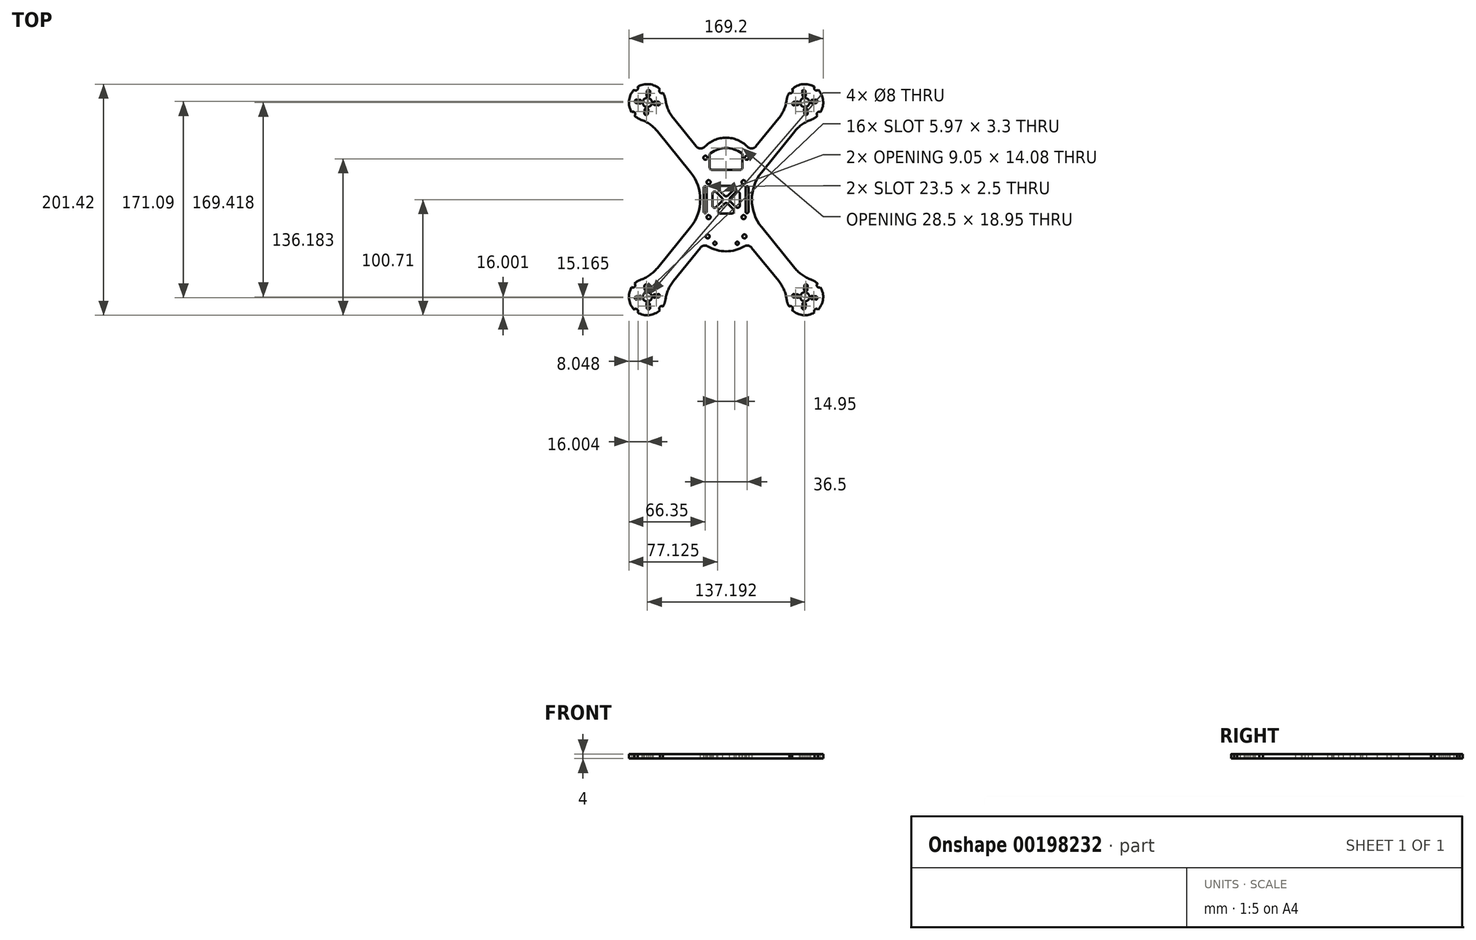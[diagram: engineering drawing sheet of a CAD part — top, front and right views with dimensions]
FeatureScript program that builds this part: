
annotation { "Feature Type Name" : "Feature", "Feature Type Description" : "" }
export const myFeature = defineFeature(function(context is Context, id is Id, definition is map)
    precondition{}
    {
        {
            var Q0;
            Q0=qCreatedBy(makeId("Top.planeOp"),FACE);
            var sketch = newSketch(context, id + "F0", { "sketchPlane" : qUnion([Q0])});
            skCircle(sketch, "E0", {"center": v(0, 0) * mm, "radius": 109 * mm, "construction": true});
            skCircle(sketch, "E1", {"center": v(68.6, 84.7) * mm, "radius": 63.5 * mm, "construction": true});
            skLineSegment(sketch, "E2", {"start": v(0, 0) * mm, "end": v(68.6, 84.7) * mm, "construction": true});
            skArc(sketch, "E3", {"start": v(73.98, 69.64) * mm, "mid": v(77.02, 71.1) * mm, "end": v(79.68, 73.17) * mm});
            skLineSegment(sketch, "E4", {"start": v(30.95, 23.91) * mm, "end": v(59.88, 59.65) * mm});
            skLineSegment(sketch, "E5", {"start": v(45.9, 70.98) * mm, "end": v(26.08, 46.5) * mm});
            skPoint(sketch, "E6.visualSharp", {"position": v(53.28, 80.1) * mm});
            skArc(sketch, "E6.filletArc", {"start": v(45.9, 70.98) * mm, "mid": v(50.4, 78.44) * mm, "end": v(52.74, 86.84) * mm});
            skPoint(sketch, "E7.visualSharp", {"position": v(67.27, 68.76) * mm});
            skArc(sketch, "E7.filletArc", {"start": v(73.98, 69.64) * mm, "mid": v(66.24, 65.61) * mm, "end": v(59.88, 59.65) * mm});
            skCircle(sketch, "E8", {"center": v(68.6, 84.7) * mm, "radius": 4 * mm});
            skLineSegment(sketch, "E9", {"start": v(0, 109) * mm, "end": v(0, 0) * mm, "construction": true});
            skLineSegment(sketch, "E10", {"start": v(0, 0) * mm, "end": v(109, 0) * mm, "construction": true});
            skArc(sketch, "E11.MirrorCS", {"start": v(-73.98, 69.64) * mm, "mid": v(-66.24, 65.61) * mm, "end": v(-59.88, 59.65) * mm});
            skArc(sketch, "E12.MirrorCS", {"start": v(-45.9, 70.98) * mm, "mid": v(-50.4, 78.44) * mm, "end": v(-52.74, 86.84) * mm});
            skPoint(sketch, "E13.MirrorP", {"position": v(-67.27, 68.76) * mm});
            skPoint(sketch, "E14.MirrorP", {"position": v(-53.28, 80.1) * mm});
            skArc(sketch, "E15.MirrorCS", {"start": v(-73.98, 69.64) * mm, "mid": v(-77.02, 71.1) * mm, "end": v(-79.68, 73.17) * mm});
            skLineSegment(sketch, "E16.MirrorCS", {"start": v(-30.95, 23.91) * mm, "end": v(-59.88, 59.65) * mm});
            skLineSegment(sketch, "E17.MirrorCS", {"start": v(-45.9, 70.98) * mm, "end": v(-26.08, 46.5) * mm});
            skCircle(sketch, "E18.MirrorC", {"center": v(-68.6, 84.7) * mm, "radius": 4 * mm});
            skCircle(sketch, "E19.MirrorC", {"center": v(-68.6, 84.7) * mm, "radius": 63.5 * mm, "construction": true});
            skLineSegment(sketch, "E20.MirrorCS", {"start": v(0, 0) * mm, "end": v(-68.6, 84.7) * mm, "construction": true});
            skArc(sketch, "E21.MirrorCS", {"start": v(-73.98, -69.64) * mm, "mid": v(-66.24, -65.61) * mm, "end": v(-59.88, -59.65) * mm});
            skArc(sketch, "E22.MirrorCS", {"start": v(-45.9, -70.98) * mm, "mid": v(-50.4, -78.44) * mm, "end": v(-52.74, -86.84) * mm});
            skPoint(sketch, "E23.MirrorP", {"position": v(-53.28, -80.1) * mm});
            skArc(sketch, "E24.MirrorCS", {"start": v(-73.98, -69.64) * mm, "mid": v(-77.02, -71.1) * mm, "end": v(-79.68, -73.17) * mm});
            skPoint(sketch, "E25.MirrorP", {"position": v(-67.27, -68.76) * mm});
            skCircle(sketch, "E26.MirrorC", {"center": v(-68.6, -84.7) * mm, "radius": 4 * mm});
            skLineSegment(sketch, "E27.MirrorCS", {"start": v(-30.95, -23.91) * mm, "end": v(-59.88, -59.65) * mm});
            skArc(sketch, "E28.MirrorCS", {"start": v(45.9, -70.98) * mm, "mid": v(50.4, -78.44) * mm, "end": v(52.74, -86.84) * mm});
            skArc(sketch, "E29.MirrorCS", {"start": v(73.98, -69.64) * mm, "mid": v(66.24, -65.61) * mm, "end": v(59.88, -59.65) * mm});
            skCircle(sketch, "E30.MirrorC", {"center": v(68.6, -84.7) * mm, "radius": 4 * mm});
            skPoint(sketch, "E31.MirrorP", {"position": v(67.27, -68.76) * mm});
            skArc(sketch, "E32.MirrorCS", {"start": v(73.98, -69.64) * mm, "mid": v(77.02, -71.1) * mm, "end": v(79.68, -73.17) * mm});
            skPoint(sketch, "E33.MirrorP", {"position": v(53.28, -80.1) * mm});
            skCircle(sketch, "E34.MirrorC", {"center": v(68.6, -84.7) * mm, "radius": 63.5 * mm, "construction": true});
            skCircle(sketch, "E35.MirrorC", {"center": v(-68.6, -84.7) * mm, "radius": 63.5 * mm, "construction": true});
            skLineSegment(sketch, "E36.MirrorCS", {"start": v(30.95, -23.91) * mm, "end": v(59.88, -59.65) * mm});
            skLineSegment(sketch, "E37.MirrorCS", {"start": v(0, 0) * mm, "end": v(-68.6, -84.7) * mm, "construction": true});
            skLineSegment(sketch, "E38.MirrorCS", {"start": v(0, 0) * mm, "end": v(68.6, -84.7) * mm, "construction": true});
            skCircle(sketch, "E39", {"center": v(-15.25, -15.25) * mm, "radius": 1.75 * mm});
            skCircle(sketch, "E40", {"center": v(15.25, -15.25) * mm, "radius": 1.75 * mm});
            skCircle(sketch, "E41.MirrorC", {"center": v(15.25, 15.25) * mm, "radius": 1.75 * mm});
            skCircle(sketch, "E42.MirrorC", {"center": v(-15.25, 15.25) * mm, "radius": 1.75 * mm});
            skLineSegment(sketch, "E43", {"start": v(-12.25, 26) * mm, "end": v(12.25, 26) * mm});
            skLineSegment(sketch, "E44", {"start": v(-14.25, 28) * mm, "end": v(-14.25, 39) * mm});
            skLineSegment(sketch, "E45", {"start": v(14.25, 28) * mm, "end": v(14.25, 39) * mm});
            skArc(sketch, "E46", {"start": v(18.61, 46.16) * mm, "mid": v(0, 54) * mm, "end": v(-18.61, 46.16) * mm});
            skPoint(sketch, "E47.visualSharp", {"position": v(-22.14, 41.64) * mm});
            skArc(sketch, "E47.filletArc", {"start": v(-26.08, 46.5) * mm, "mid": v(-22.42, 44.65) * mm, "end": v(-18.61, 46.16) * mm});
            skPoint(sketch, "E48.visualSharp", {"position": v(22.14, 41.64) * mm});
            skArc(sketch, "E48.filletArc", {"start": v(18.61, 46.16) * mm, "mid": v(22.42, 44.65) * mm, "end": v(26.08, 46.5) * mm});
            skPoint(sketch, "E49.visualSharp", {"position": v(-14.25, 26) * mm});
            skArc(sketch, "E49.filletArc", {"start": v(-14.25, 28) * mm, "mid": v(-13.66, 26.59) * mm, "end": v(-12.25, 26) * mm});
            skPoint(sketch, "E50.visualSharp", {"position": v(14.25, 26) * mm});
            skArc(sketch, "E50.filletArc", {"start": v(12.25, 26) * mm, "mid": v(13.66, 26.59) * mm, "end": v(14.25, 28) * mm});
            skPoint(sketch, "E51.visualSharp", {"position": v(-14.25, 40) * mm});
            skPoint(sketch, "E52.visualSharp", {"position": v(14.25, 44) * mm});
            skArc(sketch, "E53", {"start": v(-30.95, -23.91) * mm, "mid": v(-22.48, 0) * mm, "end": v(-30.95, 23.91) * mm});
            skArc(sketch, "E54.MirrorCS", {"start": v(30.95, -23.91) * mm, "mid": v(22.48, 0) * mm, "end": v(30.95, 23.91) * mm});
            skLineSegment(sketch, "E55", {"start": v(-45.9, -70.98) * mm, "end": v(-22.27, -41.8) * mm});
            skLineSegment(sketch, "E56", {"start": v(45.9, -70.98) * mm, "end": v(22.27, -41.8) * mm});
            skCircle(sketch, "E57", {"center": v(-16, -32) * mm, "radius": 1.75 * mm});
            skCircle(sketch, "E58.MirrorC", {"center": v(16, -32) * mm, "radius": 1.75 * mm});
            skCircle(sketch, "E59", {"center": v(-18, 36.5) * mm, "radius": 1.75 * mm});
            skCircle(sketch, "E60.MirrorC", {"center": v(18, 36.5) * mm, "radius": 1.75 * mm});
            skLineSegment(sketch, "E61.bottom", {"start": v(-19.5, 10.5) * mm, "end": v(-17, 10.5) * mm, "construction": true});
            skLineSegment(sketch, "E61.top", {"start": v(-19.5, -10.5) * mm, "end": v(-17, -10.5) * mm, "construction": true});
            skLineSegment(sketch, "E61.left", {"start": v(-19.5, 10.5) * mm, "end": v(-19.5, -10.5) * mm});
            skLineSegment(sketch, "E61.right", {"start": v(-17, 10.5) * mm, "end": v(-17, -10.5) * mm});
            skArc(sketch, "E62", {"start": v(-17, 10.5) * mm, "mid": v(-18.25, 11.75) * mm, "end": v(-19.5, 10.5) * mm});
            skArc(sketch, "E63", {"start": v(-19.5, -10.5) * mm, "mid": v(-18.25, -11.75) * mm, "end": v(-17, -10.5) * mm});
            skArc(sketch, "E64.MirrorCS", {"start": v(19.5, -10.5) * mm, "mid": v(18.25, -11.75) * mm, "end": v(17, -10.5) * mm});
            skLineSegment(sketch, "E65.MirrorCS", {"start": v(19.5, 10.5) * mm, "end": v(17, 10.5) * mm, "construction": true});
            skLineSegment(sketch, "E66.MirrorCS", {"start": v(19.5, -10.5) * mm, "end": v(17, -10.5) * mm, "construction": true});
            skLineSegment(sketch, "E67.MirrorCS", {"start": v(19.5, 10.5) * mm, "end": v(19.5, -10.5) * mm});
            skLineSegment(sketch, "E68.MirrorCS", {"start": v(17, 10.5) * mm, "end": v(17, -10.5) * mm});
            skArc(sketch, "E69.MirrorCS", {"start": v(17, 10.5) * mm, "mid": v(18.25, 11.75) * mm, "end": v(19.5, 10.5) * mm});
            skArc(sketch, "E70", {"start": v(-77.04, -98.3) * mm, "mid": v(-77.4, -95.59) * mm, "end": v(-80.14, -95.79) * mm});
            skArc(sketch, "E71", {"start": v(-82.19, -76.27) * mm, "mid": v(-79.48, -75.9) * mm, "end": v(-79.68, -73.17) * mm});
            skArc(sketch, "E72", {"start": v(-55, -93.15) * mm, "mid": v(-57.72, -93.52) * mm, "end": v(-57.51, -96.25) * mm});
            skLineSegment(sketch, "E73", {"start": v(-81.03, -74.64) * mm, "end": v(-56.16, -94.78) * mm, "construction": true});
            skArc(sketch, "E74.MirrorC", {"start": v(77.04, -98.3) * mm, "mid": v(77.4, -95.59) * mm, "end": v(80.14, -95.79) * mm});
            skArc(sketch, "E75.MirrorC", {"start": v(82.19, -76.27) * mm, "mid": v(79.48, -75.9) * mm, "end": v(79.68, -73.17) * mm});
            skArc(sketch, "E76.MirrorC", {"start": v(55, -93.15) * mm, "mid": v(57.72, -93.52) * mm, "end": v(57.51, -96.25) * mm});
            skArc(sketch, "E77.MirrorC", {"start": v(-82.19, 76.27) * mm, "mid": v(-79.48, 75.9) * mm, "end": v(-79.68, 73.17) * mm});
            skArc(sketch, "E78.MirrorC", {"start": v(-77.04, 98.3) * mm, "mid": v(-77.4, 95.59) * mm, "end": v(-80.14, 95.79) * mm});
            skArc(sketch, "E79.MirrorC", {"start": v(-55, 93.15) * mm, "mid": v(-57.72, 93.52) * mm, "end": v(-57.51, 96.25) * mm});
            skArc(sketch, "E80.MirrorC", {"start": v(82.19, 76.27) * mm, "mid": v(79.48, 75.9) * mm, "end": v(79.68, 73.17) * mm});
            skArc(sketch, "E81.MirrorC", {"start": v(77.04, 98.3) * mm, "mid": v(77.4, 95.59) * mm, "end": v(80.14, 95.79) * mm});
            skArc(sketch, "E82.MirrorC", {"start": v(55, 93.15) * mm, "mid": v(57.72, 93.52) * mm, "end": v(57.51, 96.25) * mm});
            skArc(sketch, "E83.trimOffspring", {"start": v(-77.04, 98.3) * mm, "mid": v(-66.92, 100.62) * mm, "end": v(-57.51, 96.25) * mm});
            skArc(sketch, "E84.trimOffspring", {"start": v(-82.19, 76.27) * mm, "mid": v(-84.5, 86.38) * mm, "end": v(-80.14, 95.79) * mm});
            skArc(sketch, "E85.trimOffspring", {"start": v(-55, 93.15) * mm, "mid": v(-53.54, 90.12) * mm, "end": v(-52.74, 86.84) * mm});
            skArc(sketch, "E86.trimOffspring", {"start": v(77.04, 98.3) * mm, "mid": v(66.92, 100.62) * mm, "end": v(57.51, 96.25) * mm});
            skArc(sketch, "E87.trimOffspring", {"start": v(55, 93.15) * mm, "mid": v(53.54, 90.12) * mm, "end": v(52.74, 86.84) * mm});
            skArc(sketch, "E88.trimOffspring", {"start": v(82.19, 76.27) * mm, "mid": v(84.5, 86.38) * mm, "end": v(80.14, 95.79) * mm});
            skArc(sketch, "E89.trimOffspring", {"start": v(-55.46, -93.84) * mm, "mid": v(-53.68, -90.5) * mm, "end": v(-52.74, -86.84) * mm});
            skArc(sketch, "E90.trimOffspring", {"start": v(-77.04, -98.3) * mm, "mid": v(-66.92, -100.62) * mm, "end": v(-57.51, -96.25) * mm});
            skLineSegment(sketch, "E91", {"start": v(-68.6, -84.7) * mm, "end": v(-78.67, -97.14) * mm, "construction": true});
            skArc(sketch, "E92.trimOffspring", {"start": v(-82.19, -76.27) * mm, "mid": v(-84.5, -86.38) * mm, "end": v(-80.14, -95.79) * mm});
            skArc(sketch, "E93.trimOffspring", {"start": v(82.19, -76.27) * mm, "mid": v(84.5, -86.38) * mm, "end": v(80.14, -95.79) * mm});
            skArc(sketch, "E94.trimOffspring", {"start": v(55, -93.15) * mm, "mid": v(53.54, -90.12) * mm, "end": v(52.74, -86.84) * mm});
            skArc(sketch, "E95.trimOffspring", {"start": v(77.04, -98.3) * mm, "mid": v(66.92, -100.62) * mm, "end": v(57.51, -96.25) * mm});
            skArc(sketch, "E96", {"start": v(13.42, 40.63) * mm, "mid": v(0, 44.95) * mm, "end": v(-13.42, 40.63) * mm});
            skArc(sketch, "E97.filletArc", {"start": v(-13.42, 40.63) * mm, "mid": v(-14.03, 39.92) * mm, "end": v(-14.25, 39) * mm});
            skPoint(sketch, "E98.visualSharp", {"position": v(14.25, 40) * mm});
            skArc(sketch, "E98.filletArc", {"start": v(14.25, 39) * mm, "mid": v(14.03, 39.92) * mm, "end": v(13.42, 40.63) * mm});
            skLineSegment(sketch, "E99", {"start": v(68.6, -84.7) * mm, "end": v(70.27, -68.8) * mm, "construction": true});
            skArc(sketch, "E100", {"start": v(67.78, -78.09) * mm, "mid": v(69.12, -79.74) * mm, "end": v(70.77, -78.4) * mm});
            skArc(sketch, "E101", {"start": v(71.08, -75.42) * mm, "mid": v(69.75, -73.77) * mm, "end": v(68.1, -75.1) * mm});
            skLineSegment(sketch, "E102", {"start": v(70.77, -78.4) * mm, "end": v(71.08, -75.42) * mm});
            skLineSegment(sketch, "E103", {"start": v(67.78, -78.09) * mm, "end": v(68.1, -75.1) * mm});
            skArc(sketch, "E104.1.0", {"start": v(61.97, -85.52) * mm, "mid": v(63.62, -84.19) * mm, "end": v(62.29, -82.54) * mm});
            skLineSegment(sketch, "E104.1.1", {"start": v(61.97, -85.52) * mm, "end": v(59, -85.2) * mm});
            skArc(sketch, "E104.1.2", {"start": v(59.3, -82.22) * mm, "mid": v(57.66, -83.56) * mm, "end": v(59, -85.2) * mm});
            skLineSegment(sketch, "E104.1.3", {"start": v(62.29, -82.54) * mm, "end": v(59.3, -82.22) * mm});
            skLineSegment(sketch, "E104.1.4", {"start": v(68.6, -84.7) * mm, "end": v(52.68, -83.04) * mm, "construction": true});
            skArc(sketch, "E104.2.0", {"start": v(69.4, -91.33) * mm, "mid": v(68.07, -89.68) * mm, "end": v(66.42, -91.02) * mm});
            skLineSegment(sketch, "E104.2.1", {"start": v(69.4, -91.33) * mm, "end": v(69.1, -94.31) * mm});
            skArc(sketch, "E104.2.2", {"start": v(66.11, -94) * mm, "mid": v(67.45, -95.65) * mm, "end": v(69.1, -94.31) * mm});
            skLineSegment(sketch, "E104.2.3", {"start": v(66.42, -91.02) * mm, "end": v(66.11, -94) * mm});
            skLineSegment(sketch, "E104.2.4", {"start": v(68.6, -84.7) * mm, "end": v(66.92, -100.62) * mm, "construction": true});
            skArc(sketch, "E104.3.0", {"start": v(75.22, -83.9) * mm, "mid": v(73.57, -85.23) * mm, "end": v(74.9, -86.88) * mm});
            skLineSegment(sketch, "E104.3.1", {"start": v(75.22, -83.9) * mm, "end": v(78.2, -84.21) * mm});
            skArc(sketch, "E104.3.2", {"start": v(77.89, -87.2) * mm, "mid": v(79.54, -85.86) * mm, "end": v(78.2, -84.21) * mm});
            skLineSegment(sketch, "E104.3.3", {"start": v(74.9, -86.88) * mm, "end": v(77.89, -87.2) * mm});
            skLineSegment(sketch, "E104.3.4", {"start": v(68.6, -84.7) * mm, "end": v(84.5, -86.38) * mm, "construction": true});
            skLineSegment(sketch, "E105.MirrorCS", {"start": v(-69.4, -91.33) * mm, "end": v(-69.1, -94.31) * mm});
            skArc(sketch, "E106.MirrorCS", {"start": v(-69.4, -91.33) * mm, "mid": v(-68.07, -89.68) * mm, "end": v(-66.42, -91.02) * mm});
            skLineSegment(sketch, "E107.MirrorCS", {"start": v(-66.42, -91.02) * mm, "end": v(-66.11, -94) * mm});
            skArc(sketch, "E108.MirrorCS", {"start": v(-66.11, -94) * mm, "mid": v(-67.45, -95.65) * mm, "end": v(-69.1, -94.31) * mm});
            skLineSegment(sketch, "E109.MirrorCS", {"start": v(-68.6, -84.7) * mm, "end": v(-66.92, -100.62) * mm, "construction": true});
            skLineSegment(sketch, "E110.MirrorCS", {"start": v(-68.6, -84.7) * mm, "end": v(-84.5, -86.38) * mm, "construction": true});
            skLineSegment(sketch, "E111.MirrorCS", {"start": v(-68.6, -84.7) * mm, "end": v(-52.68, -83.04) * mm, "construction": true});
            skLineSegment(sketch, "E112.MirrorCS", {"start": v(-68.6, -84.7) * mm, "end": v(-70.27, -68.8) * mm, "construction": true});
            skLineSegment(sketch, "E113.MirrorCS", {"start": v(-70.77, -78.4) * mm, "end": v(-71.08, -75.42) * mm});
            skLineSegment(sketch, "E114.MirrorCS", {"start": v(-67.78, -78.09) * mm, "end": v(-68.1, -75.1) * mm});
            skArc(sketch, "E115.MirrorCS", {"start": v(-71.08, -75.42) * mm, "mid": v(-69.75, -73.77) * mm, "end": v(-68.1, -75.1) * mm});
            skArc(sketch, "E116.MirrorCS", {"start": v(-67.78, -78.09) * mm, "mid": v(-69.12, -79.74) * mm, "end": v(-70.77, -78.4) * mm});
            skLineSegment(sketch, "E117.MirrorCS", {"start": v(-75.22, -83.9) * mm, "end": v(-78.2, -84.21) * mm});
            skArc(sketch, "E118.MirrorCS", {"start": v(-77.89, -87.2) * mm, "mid": v(-79.54, -85.86) * mm, "end": v(-78.2, -84.21) * mm});
            skLineSegment(sketch, "E119.MirrorCS", {"start": v(-74.9, -86.88) * mm, "end": v(-77.89, -87.2) * mm});
            skArc(sketch, "E120.MirrorCS", {"start": v(-75.22, -83.9) * mm, "mid": v(-73.57, -85.23) * mm, "end": v(-74.9, -86.88) * mm});
            skLineSegment(sketch, "E121.MirrorCS", {"start": v(-61.97, -85.52) * mm, "end": v(-59, -85.2) * mm});
            skArc(sketch, "E122.MirrorCS", {"start": v(-59.3, -82.22) * mm, "mid": v(-57.66, -83.56) * mm, "end": v(-59, -85.2) * mm});
            skLineSegment(sketch, "E123.MirrorCS", {"start": v(-62.29, -82.54) * mm, "end": v(-59.3, -82.22) * mm});
            skArc(sketch, "E124.MirrorCS", {"start": v(-61.97, -85.52) * mm, "mid": v(-63.62, -84.19) * mm, "end": v(-62.29, -82.54) * mm});
            skArc(sketch, "E125.MirrorCS", {"start": v(-75.22, 83.9) * mm, "mid": v(-73.57, 85.23) * mm, "end": v(-74.9, 86.88) * mm});
            skLineSegment(sketch, "E126.MirrorCS", {"start": v(-74.9, 86.88) * mm, "end": v(-77.89, 87.2) * mm});
            skArc(sketch, "E127.MirrorCS", {"start": v(-77.89, 87.2) * mm, "mid": v(-79.54, 85.86) * mm, "end": v(-78.2, 84.21) * mm});
            skLineSegment(sketch, "E128.MirrorCS", {"start": v(-75.22, 83.9) * mm, "end": v(-78.2, 84.21) * mm});
            skLineSegment(sketch, "E129.MirrorCS", {"start": v(-68.6, 84.7) * mm, "end": v(-84.5, 86.38) * mm, "construction": true});
            skLineSegment(sketch, "E130.MirrorCS", {"start": v(-68.6, 84.7) * mm, "end": v(-70.27, 68.8) * mm, "construction": true});
            skLineSegment(sketch, "E131.MirrorCS", {"start": v(-68.6, 84.7) * mm, "end": v(-52.68, 83.04) * mm, "construction": true});
            skLineSegment(sketch, "E132.MirrorCS", {"start": v(-68.6, 84.7) * mm, "end": v(-66.92, 100.62) * mm, "construction": true});
            skArc(sketch, "E133.MirrorCS", {"start": v(-67.78, 78.09) * mm, "mid": v(-69.12, 79.74) * mm, "end": v(-70.77, 78.4) * mm});
            skLineSegment(sketch, "E134.MirrorCS", {"start": v(-70.77, 78.4) * mm, "end": v(-71.08, 75.42) * mm});
            skLineSegment(sketch, "E135.MirrorCS", {"start": v(-67.78, 78.09) * mm, "end": v(-68.1, 75.1) * mm});
            skArc(sketch, "E136.MirrorCS", {"start": v(-71.08, 75.42) * mm, "mid": v(-69.75, 73.77) * mm, "end": v(-68.1, 75.1) * mm});
            skArc(sketch, "E137.MirrorCS", {"start": v(-61.97, 85.52) * mm, "mid": v(-63.62, 84.19) * mm, "end": v(-62.29, 82.54) * mm});
            skLineSegment(sketch, "E138.MirrorCS", {"start": v(-61.97, 85.52) * mm, "end": v(-59, 85.2) * mm});
            skLineSegment(sketch, "E139.MirrorCS", {"start": v(-62.29, 82.54) * mm, "end": v(-59.3, 82.22) * mm});
            skArc(sketch, "E140.MirrorCS", {"start": v(-59.3, 82.22) * mm, "mid": v(-57.66, 83.56) * mm, "end": v(-59, 85.2) * mm});
            skLineSegment(sketch, "E141.MirrorCS", {"start": v(-69.4, 91.33) * mm, "end": v(-69.1, 94.31) * mm});
            skArc(sketch, "E142.MirrorCS", {"start": v(-66.11, 94) * mm, "mid": v(-67.45, 95.65) * mm, "end": v(-69.1, 94.31) * mm});
            skLineSegment(sketch, "E143.MirrorCS", {"start": v(-66.42, 91.02) * mm, "end": v(-66.11, 94) * mm});
            skArc(sketch, "E144.MirrorCS", {"start": v(-69.4, 91.33) * mm, "mid": v(-68.07, 89.68) * mm, "end": v(-66.42, 91.02) * mm});
            skLineSegment(sketch, "E145.MirrorCS", {"start": v(66.42, 91.02) * mm, "end": v(66.11, 94) * mm});
            skArc(sketch, "E146.MirrorCS", {"start": v(66.11, 94) * mm, "mid": v(67.45, 95.65) * mm, "end": v(69.1, 94.31) * mm});
            skLineSegment(sketch, "E147.MirrorCS", {"start": v(69.4, 91.33) * mm, "end": v(69.1, 94.31) * mm});
            skArc(sketch, "E148.MirrorCS", {"start": v(69.4, 91.33) * mm, "mid": v(68.07, 89.68) * mm, "end": v(66.42, 91.02) * mm});
            skLineSegment(sketch, "E149.MirrorCS", {"start": v(75.22, 83.9) * mm, "end": v(78.2, 84.21) * mm});
            skArc(sketch, "E150.MirrorCS", {"start": v(77.89, 87.2) * mm, "mid": v(79.54, 85.86) * mm, "end": v(78.2, 84.21) * mm});
            skArc(sketch, "E151.MirrorCS", {"start": v(75.22, 83.9) * mm, "mid": v(73.57, 85.23) * mm, "end": v(74.9, 86.88) * mm});
            skLineSegment(sketch, "E152.MirrorCS", {"start": v(74.9, 86.88) * mm, "end": v(77.89, 87.2) * mm});
            skLineSegment(sketch, "E153.MirrorCS", {"start": v(70.77, 78.4) * mm, "end": v(71.08, 75.42) * mm});
            skArc(sketch, "E154.MirrorCS", {"start": v(71.08, 75.42) * mm, "mid": v(69.75, 73.77) * mm, "end": v(68.1, 75.1) * mm});
            skLineSegment(sketch, "E155.MirrorCS", {"start": v(68.6, 84.7) * mm, "end": v(70.27, 68.8) * mm, "construction": true});
            skLineSegment(sketch, "E156.MirrorCS", {"start": v(67.78, 78.09) * mm, "end": v(68.1, 75.1) * mm});
            skArc(sketch, "E157.MirrorCS", {"start": v(67.78, 78.09) * mm, "mid": v(69.12, 79.74) * mm, "end": v(70.77, 78.4) * mm});
            skArc(sketch, "E158.MirrorCS", {"start": v(59.3, 82.22) * mm, "mid": v(57.66, 83.56) * mm, "end": v(59, 85.2) * mm});
            skLineSegment(sketch, "E159.MirrorCS", {"start": v(62.29, 82.54) * mm, "end": v(59.3, 82.22) * mm});
            skLineSegment(sketch, "E160.MirrorCS", {"start": v(61.97, 85.52) * mm, "end": v(59, 85.2) * mm});
            skArc(sketch, "E161.MirrorCS", {"start": v(61.97, 85.52) * mm, "mid": v(63.62, 84.19) * mm, "end": v(62.29, 82.54) * mm});
            skLineSegment(sketch, "E162.MirrorCS", {"start": v(68.6, 84.7) * mm, "end": v(84.5, 86.38) * mm, "construction": true});
            skLineSegment(sketch, "E163.MirrorCS", {"start": v(68.6, 84.7) * mm, "end": v(66.92, 100.62) * mm, "construction": true});
            skLineSegment(sketch, "E164.MirrorCS", {"start": v(68.6, 84.7) * mm, "end": v(52.68, 83.04) * mm, "construction": true});
            skCircle(sketch, "E165", {"center": v(16, -32) * mm, "radius": 2.5 * mm, "construction": true});
            skArc(sketch, "E166.trimOffspring", {"start": v(-15.83, -40.65) * mm, "mid": v(0, -45) * mm, "end": v(15.83, -40.65) * mm});
            skPoint(sketch, "E167.visualSharp", {"position": v(-4.3, -19.62) * mm});
            skPoint(sketch, "E168.MirrorP", {"position": v(4.3, -19.62) * mm});
            skCircle(sketch, "E169", {"center": v(-9.75, -38) * mm, "radius": 1.35 * mm});
            skCircle(sketch, "E170.MirrorC", {"center": v(9.75, -38) * mm, "radius": 1.35 * mm});
            skCircle(sketch, "E171", {"center": v(9.75, -38) * mm, "radius": 2.75 * mm, "construction": true});
            skPoint(sketch, "E172.visualSharp", {"position": v(-19.36, -38.21) * mm});
            skArc(sketch, "E172.filletArc", {"start": v(-15.83, -40.65) * mm, "mid": v(-19.27, -40.03) * mm, "end": v(-22.27, -41.8) * mm});
            skPoint(sketch, "E173.visualSharp", {"position": v(19.36, -38.21) * mm});
            skArc(sketch, "E173.filletArc", {"start": v(22.27, -41.8) * mm, "mid": v(19.27, -40.03) * mm, "end": v(15.83, -40.65) * mm});
            skSolve(sketch);
        }
        {
            var Q0;
            Q0=qSketchRegion(id+"F0",true);
            var Q1;
            Q1=makeQuery(id+"F0.imprint","IMPRINT",FACE,{"disambiguationData":[TD([[makeQuery(id+"F0.imprint","IMPRINT",EDGE,{"derivedFrom":sQuery(id+"F0.wireOp",EDGE,"1dedc878-54b1-44d6-bfa4-69265974a363.sketch_text.stroke-27")}),-1.0]])]});
            var Q2;
            Q2=makeQuery(id+"F0.imprint","IMPRINT",FACE,{"disambiguationData":[TD([[makeQuery(id+"F0.imprint","IMPRINT",EDGE,{"derivedFrom":sQuery(id+"F0.wireOp",EDGE,"1dedc878-54b1-44d6-bfa4-69265974a363.sketch_text.stroke-0")}),-1.0]])]});
            extrude(context, id + "F1", {"entities" : qUnion([Q0, Q1, Q2]), "depth" : 4 * mm});
        }
        {
            var Q0;
            Q0=makeQuery(id+"F1.opExtrude","CAP_FACE",FACE,{"disambiguationData":[OSD([sQuery(id+"F0.wireOp",EDGE,"E3"),sQuery(id+"F0.wireOp",EDGE,"E4"),sQuery(id+"F0.wireOp",EDGE,"E5"),sQuery(id+"F0.wireOp",EDGE,"E6.filletArc"),sQuery(id+"F0.wireOp",EDGE,"E7.filletArc"),sQuery(id+"F0.wireOp",EDGE,"E11.MirrorCS"),sQuery(id+"F0.wireOp",EDGE,"E12.MirrorCS"),sQuery(id+"F0.wireOp",EDGE,"E15.MirrorCS"),sQuery(id+"F0.wireOp",EDGE,"E16.MirrorCS"),sQuery(id+"F0.wireOp",EDGE,"E17.MirrorCS"),sQuery(id+"F0.wireOp",EDGE,"E18.MirrorC"),sQuery(id+"F0.wireOp",EDGE,"E21.MirrorCS"),sQuery(id+"F0.wireOp",EDGE,"E22.MirrorCS"),sQuery(id+"F0.wireOp",EDGE,"E24.MirrorCS"),sQuery(id+"F0.wireOp",EDGE,"E26.MirrorC"),sQuery(id+"F0.wireOp",EDGE,"E27.MirrorCS"),sQuery(id+"F0.wireOp",EDGE,"E28.MirrorCS"),sQuery(id+"F0.wireOp",EDGE,"E29.MirrorCS"),sQuery(id+"F0.wireOp",EDGE,"E30.MirrorC"),sQuery(id+"F0.wireOp",EDGE,"E32.MirrorCS"),sQuery(id+"F0.wireOp",EDGE,"E36.MirrorCS"),sQuery(id+"F0.wireOp",EDGE,"E39"),sQuery(id+"F0.wireOp",EDGE,"E40"),sQuery(id+"F0.wireOp",EDGE,"E41.MirrorC"),sQuery(id+"F0.wireOp",EDGE,"E42.MirrorC"),sQuery(id+"F0.wireOp",EDGE,"E43"),sQuery(id+"F0.wireOp",EDGE,"E44"),sQuery(id+"F0.wireOp",EDGE,"E45"),sQuery(id+"F0.wireOp",EDGE,"E46"),sQuery(id+"F0.wireOp",EDGE,"E47.filletArc"),sQuery(id+"F0.wireOp",EDGE,"E48.filletArc"),sQuery(id+"F0.wireOp",EDGE,"E49.filletArc"),sQuery(id+"F0.wireOp",EDGE,"E50.filletArc"),sQuery(id+"F0.wireOp",EDGE,"E53"),sQuery(id+"F0.wireOp",EDGE,"E54.MirrorCS"),sQuery(id+"F0.wireOp",EDGE,"E55"),sQuery(id+"F0.wireOp",EDGE,"E56"),sQuery(id+"F0.wireOp",EDGE,"E57"),sQuery(id+"F0.wireOp",EDGE,"E58.MirrorC"),sQuery(id+"F0.wireOp",EDGE,"E59"),sQuery(id+"F0.wireOp",EDGE,"E60.MirrorC"),sQuery(id+"F0.wireOp",EDGE,"E61.left"),sQuery(id+"F0.wireOp",EDGE,"E61.right"),sQuery(id+"F0.wireOp",EDGE,"E62"),sQuery(id+"F0.wireOp",EDGE,"E63"),sQuery(id+"F0.wireOp",EDGE,"E64.MirrorCS"),sQuery(id+"F0.wireOp",EDGE,"E67.MirrorCS"),sQuery(id+"F0.wireOp",EDGE,"E68.MirrorCS"),sQuery(id+"F0.wireOp",EDGE,"E69.MirrorCS"),sQuery(id+"F0.wireOp",EDGE,"E70"),sQuery(id+"F0.wireOp",EDGE,"E71"),sQuery(id+"F0.wireOp",EDGE,"E72"),sQuery(id+"F0.wireOp",EDGE,"E74.MirrorC"),sQuery(id+"F0.wireOp",EDGE,"E75.MirrorC"),sQuery(id+"F0.wireOp",EDGE,"E76.MirrorC"),sQuery(id+"F0.wireOp",EDGE,"E77.MirrorC"),sQuery(id+"F0.wireOp",EDGE,"E78.MirrorC"),sQuery(id+"F0.wireOp",EDGE,"E79.MirrorC"),sQuery(id+"F0.wireOp",EDGE,"E80.MirrorC"),sQuery(id+"F0.wireOp",EDGE,"E81.MirrorC"),sQuery(id+"F0.wireOp",EDGE,"E82.MirrorC"),sQuery(id+"F0.wireOp",EDGE,"E83.trimOffspring"),sQuery(id+"F0.wireOp",EDGE,"E84.trimOffspring"),sQuery(id+"F0.wireOp",EDGE,"E85.trimOffspring"),sQuery(id+"F0.wireOp",EDGE,"E86.trimOffspring"),sQuery(id+"F0.wireOp",EDGE,"E87.trimOffspring"),sQuery(id+"F0.wireOp",EDGE,"E88.trimOffspring"),sQuery(id+"F0.wireOp",EDGE,"E89.trimOffspring"),sQuery(id+"F0.wireOp",EDGE,"E90.trimOffspring"),sQuery(id+"F0.wireOp",EDGE,"E92.trimOffspring"),sQuery(id+"F0.wireOp",EDGE,"E93.trimOffspring"),sQuery(id+"F0.wireOp",EDGE,"E94.trimOffspring"),sQuery(id+"F0.wireOp",EDGE,"E95.trimOffspring"),sQuery(id+"F0.wireOp",EDGE,"E96"),sQuery(id+"F0.wireOp",EDGE,"E97.filletArc"),sQuery(id+"F0.wireOp",EDGE,"E98.filletArc"),sQuery(id+"F0.wireOp",EDGE,"E100"),sQuery(id+"F0.wireOp",EDGE,"E101"),sQuery(id+"F0.wireOp",EDGE,"E102"),sQuery(id+"F0.wireOp",EDGE,"E103"),sQuery(id+"F0.wireOp",EDGE,"E104.1.0"),sQuery(id+"F0.wireOp",EDGE,"E104.1.1"),sQuery(id+"F0.wireOp",EDGE,"E104.1.2"),sQuery(id+"F0.wireOp",EDGE,"E104.1.3"),sQuery(id+"F0.wireOp",EDGE,"E104.2.0"),sQuery(id+"F0.wireOp",EDGE,"E104.2.1"),sQuery(id+"F0.wireOp",EDGE,"E104.2.2"),sQuery(id+"F0.wireOp",EDGE,"E104.2.3"),sQuery(id+"F0.wireOp",EDGE,"E104.3.0"),sQuery(id+"F0.wireOp",EDGE,"E104.3.1"),sQuery(id+"F0.wireOp",EDGE,"E104.3.2"),sQuery(id+"F0.wireOp",EDGE,"E104.3.3"),sQuery(id+"F0.wireOp",EDGE,"E105.MirrorCS"),sQuery(id+"F0.wireOp",EDGE,"E106.MirrorCS"),sQuery(id+"F0.wireOp",EDGE,"E107.MirrorCS"),sQuery(id+"F0.wireOp",EDGE,"E108.MirrorCS"),sQuery(id+"F0.wireOp",EDGE,"E113.MirrorCS"),sQuery(id+"F0.wireOp",EDGE,"E114.MirrorCS"),sQuery(id+"F0.wireOp",EDGE,"E115.MirrorCS"),sQuery(id+"F0.wireOp",EDGE,"E116.MirrorCS"),sQuery(id+"F0.wireOp",EDGE,"E117.MirrorCS"),sQuery(id+"F0.wireOp",EDGE,"E118.MirrorCS"),sQuery(id+"F0.wireOp",EDGE,"E119.MirrorCS"),sQuery(id+"F0.wireOp",EDGE,"E120.MirrorCS"),sQuery(id+"F0.wireOp",EDGE,"E121.MirrorCS"),sQuery(id+"F0.wireOp",EDGE,"E122.MirrorCS"),sQuery(id+"F0.wireOp",EDGE,"E123.MirrorCS"),sQuery(id+"F0.wireOp",EDGE,"E124.MirrorCS"),sQuery(id+"F0.wireOp",EDGE,"E125.MirrorCS"),sQuery(id+"F0.wireOp",EDGE,"E126.MirrorCS"),sQuery(id+"F0.wireOp",EDGE,"E127.MirrorCS"),sQuery(id+"F0.wireOp",EDGE,"E128.MirrorCS"),sQuery(id+"F0.wireOp",EDGE,"E133.MirrorCS"),sQuery(id+"F0.wireOp",EDGE,"E134.MirrorCS"),sQuery(id+"F0.wireOp",EDGE,"E135.MirrorCS"),sQuery(id+"F0.wireOp",EDGE,"E136.MirrorCS"),sQuery(id+"F0.wireOp",EDGE,"E137.MirrorCS"),sQuery(id+"F0.wireOp",EDGE,"E138.MirrorCS"),sQuery(id+"F0.wireOp",EDGE,"E139.MirrorCS"),sQuery(id+"F0.wireOp",EDGE,"E140.MirrorCS"),sQuery(id+"F0.wireOp",EDGE,"E141.MirrorCS"),sQuery(id+"F0.wireOp",EDGE,"E142.MirrorCS"),sQuery(id+"F0.wireOp",EDGE,"E143.MirrorCS"),sQuery(id+"F0.wireOp",EDGE,"E144.MirrorCS"),sQuery(id+"F0.wireOp",EDGE,"E145.MirrorCS"),sQuery(id+"F0.wireOp",EDGE,"E146.MirrorCS"),sQuery(id+"F0.wireOp",EDGE,"E147.MirrorCS"),sQuery(id+"F0.wireOp",EDGE,"E148.MirrorCS"),sQuery(id+"F0.wireOp",EDGE,"E149.MirrorCS"),sQuery(id+"F0.wireOp",EDGE,"E150.MirrorCS"),sQuery(id+"F0.wireOp",EDGE,"E151.MirrorCS"),sQuery(id+"F0.wireOp",EDGE,"E152.MirrorCS"),sQuery(id+"F0.wireOp",EDGE,"E153.MirrorCS"),sQuery(id+"F0.wireOp",EDGE,"E154.MirrorCS"),sQuery(id+"F0.wireOp",EDGE,"E8"),sQuery(id+"F0.wireOp",EDGE,"E156.MirrorCS"),sQuery(id+"F0.wireOp",EDGE,"E157.MirrorCS"),sQuery(id+"F0.wireOp",EDGE,"E158.MirrorCS"),sQuery(id+"F0.wireOp",EDGE,"E159.MirrorCS"),sQuery(id+"F0.wireOp",EDGE,"E160.MirrorCS"),sQuery(id+"F0.wireOp",EDGE,"E161.MirrorCS"),sQuery(id+"F0.wireOp",EDGE,"E166.trimOffspring"),sQuery(id+"F0.wireOp",EDGE,"E169"),sQuery(id+"F0.wireOp",EDGE,"E170.MirrorC"),sQuery(id+"F0.wireOp",EDGE,"E172.filletArc"),sQuery(id+"F0.wireOp",EDGE,"E173.filletArc")])],"isStart":false});
            var sketch = newSketch(context, id + "F2", { "sketchPlane" : qUnion([Q0])});
            skLineSegment(sketch, "E174.bottom", {"start": v(-5.05, 12) * mm, "end": v(5.05, 12) * mm});
            skLineSegment(sketch, "E174.top", {"start": v(-5.05, -12) * mm, "end": v(5.05, -12) * mm});
            skLineSegment(sketch, "E174.left", {"start": v(-12, 5.05) * mm, "end": v(-12, -5.05) * mm});
            skLineSegment(sketch, "E174.right", {"start": v(12, 5.05) * mm, "end": v(12, -5.05) * mm});
            skLineSegment(sketch, "E175", {"start": v(-12, 12) * mm, "end": v(12, -12) * mm, "construction": true});
            skLineSegment(sketch, "E176", {"start": v(-12, -12) * mm, "end": v(12, 12) * mm, "construction": true});
            skLineSegment(sketch, "E177", {"start": v(-8.59, 6.46) * mm, "end": v(-3.54, 1.41) * mm});
            skLineSegment(sketch, "E178", {"start": v(-6.46, 8.59) * mm, "end": v(-1.41, 3.54) * mm});
            skLineSegment(sketch, "E179.MirrorCS", {"start": v(6.46, 8.59) * mm, "end": v(1.41, 3.54) * mm});
            skLineSegment(sketch, "E180.MirrorCS", {"start": v(8.59, 6.46) * mm, "end": v(3.54, 1.41) * mm});
            skLineSegment(sketch, "E181.trimOffspring", {"start": v(-3.54, -1.41) * mm, "end": v(-8.59, -6.46) * mm});
            skLineSegment(sketch, "E182.trimOffspring", {"start": v(1.41, -3.54) * mm, "end": v(6.46, -8.59) * mm});
            skLineSegment(sketch, "E183.trimOffspring", {"start": v(-1.41, -3.54) * mm, "end": v(-6.46, -8.59) * mm});
            skLineSegment(sketch, "E184.trimOffspring", {"start": v(3.54, -1.41) * mm, "end": v(8.59, -6.46) * mm});
            skPoint(sketch, "E185.visualSharp", {"position": v(-9.88, 12) * mm});
            skArc(sketch, "E185.filletArc", {"start": v(-5.05, 12) * mm, "mid": v(-6.9, 10.77) * mm, "end": v(-6.46, 8.59) * mm});
            skPoint(sketch, "E186.visualSharp", {"position": v(9.88, 12) * mm});
            skArc(sketch, "E186.filletArc", {"start": v(6.46, 8.59) * mm, "mid": v(6.9, 10.77) * mm, "end": v(5.05, 12) * mm});
            skPoint(sketch, "E187.visualSharp", {"position": v(0, 2.12) * mm});
            skArc(sketch, "E187.filletArc", {"start": v(-1.41, 3.54) * mm, "mid": v(0, 2.95) * mm, "end": v(1.41, 3.54) * mm});
            skPoint(sketch, "E188.visualSharp", {"position": v(-2.12, 0) * mm});
            skArc(sketch, "E188.filletArc", {"start": v(-3.54, -1.41) * mm, "mid": v(-2.95, 0) * mm, "end": v(-3.54, 1.41) * mm});
            skPoint(sketch, "E189.visualSharp", {"position": v(-12, 9.88) * mm});
            skArc(sketch, "E189.filletArc", {"start": v(-8.59, 6.46) * mm, "mid": v(-10.77, 6.9) * mm, "end": v(-12, 5.05) * mm});
            skPoint(sketch, "E190.visualSharp", {"position": v(-12, -9.88) * mm});
            skArc(sketch, "E190.filletArc", {"start": v(-12, -5.05) * mm, "mid": v(-10.77, -6.9) * mm, "end": v(-8.59, -6.46) * mm});
            skPoint(sketch, "E191.visualSharp", {"position": v(-9.88, -12) * mm});
            skArc(sketch, "E191.filletArc", {"start": v(-6.46, -8.59) * mm, "mid": v(-6.9, -10.77) * mm, "end": v(-5.05, -12) * mm});
            skPoint(sketch, "E192.visualSharp", {"position": v(9.88, -12) * mm});
            skArc(sketch, "E192.filletArc", {"start": v(5.05, -12) * mm, "mid": v(6.9, -10.77) * mm, "end": v(6.46, -8.59) * mm});
            skPoint(sketch, "E193.visualSharp", {"position": v(0, -2.12) * mm});
            skArc(sketch, "E193.filletArc", {"start": v(1.41, -3.54) * mm, "mid": v(0, -2.95) * mm, "end": v(-1.41, -3.54) * mm});
            skPoint(sketch, "E194.visualSharp", {"position": v(2.12, 0) * mm});
            skArc(sketch, "E194.filletArc", {"start": v(3.54, 1.41) * mm, "mid": v(2.95, 0) * mm, "end": v(3.54, -1.41) * mm});
            skPoint(sketch, "E195.visualSharp", {"position": v(12, -9.88) * mm});
            skArc(sketch, "E195.filletArc", {"start": v(8.59, -6.46) * mm, "mid": v(10.77, -6.9) * mm, "end": v(12, -5.05) * mm});
            skPoint(sketch, "E196.visualSharp", {"position": v(12, 9.88) * mm});
            skArc(sketch, "E196.filletArc", {"start": v(12, 5.05) * mm, "mid": v(10.77, 6.9) * mm, "end": v(8.59, 6.46) * mm});
            skSolve(sketch);
        }
        {
            var Q0;
            Q0 = qSketchRegion(id + "F2", true);
            extrude(context, id + "F3", {"entities" : qUnion([Q0]), "operationType" : NewBodyOperationType.REMOVE, "oppositeDirection" : true, "depth" : 25 * mm});
        }
    });
